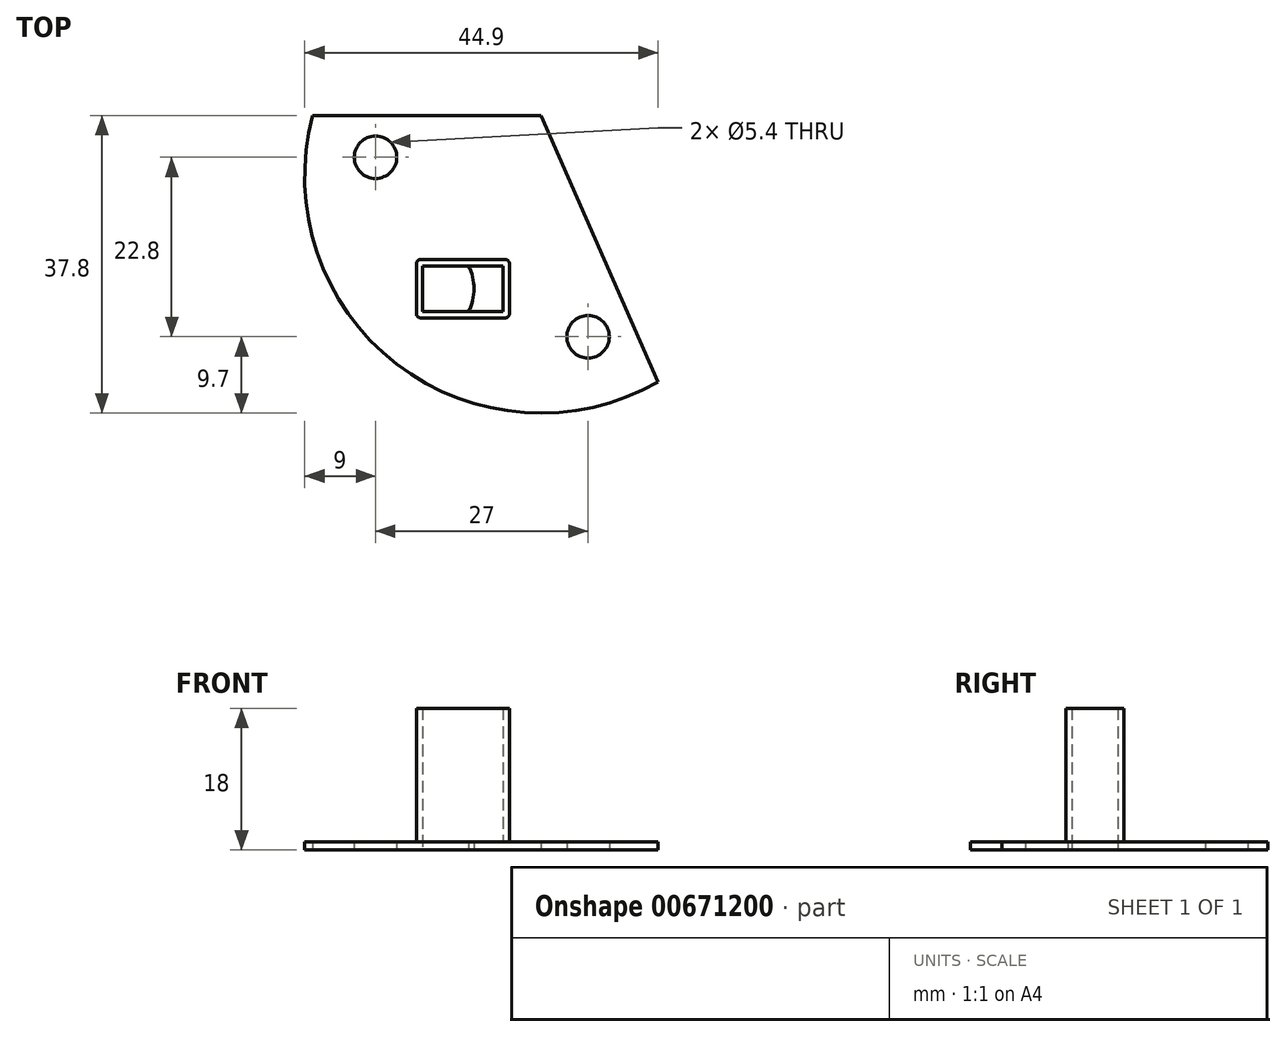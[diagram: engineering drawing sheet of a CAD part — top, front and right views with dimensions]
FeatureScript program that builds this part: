
annotation { "Feature Type Name" : "Feature", "Feature Type Description" : "" }
export const myFeature = defineFeature(function(context is Context, id is Id, definition is map)
    precondition{}
    {
        {
            var Q0;
            Q0=qCreatedBy(makeId("Top.planeOp"),FACE);
            var sketch = newSketch(context, id + "F0", { "sketchPlane" : qUnion([Q0])});
            skArc(sketch, "E0", {"start": v(-28.97, 7.8) * mm, "mid": v(-18.32, -23.75) * mm, "end": v(14.9, -26.04) * mm});
            skCircle(sketch, "E1", {"center": v(-21, 2.5) * mm, "radius": 2.7 * mm});
            skCircle(sketch, "E2", {"center": v(6, -20.3) * mm, "radius": 2.7 * mm});
            skCircle(sketch, "E3", {"center": v(-15, -14.2) * mm, "radius": 6.5 * mm});
            skLineSegment(sketch, "E4", {"start": v(-28.97, 7.8) * mm, "end": v(0, 7.8) * mm});
            skLineSegment(sketch, "E5", {"start": v(0, 7.8) * mm, "end": v(14.9, -26.04) * mm});
            skLineSegment(sketch, "E6.bottom", {"start": v(-15, -11.3) * mm, "end": v(-4.8, -11.3) * mm});
            skLineSegment(sketch, "E6.top", {"start": v(-15, -17.1) * mm, "end": v(-4.8, -17.1) * mm});
            skLineSegment(sketch, "E6.left", {"start": v(-15, -11.3) * mm, "end": v(-15, -17.1) * mm});
            skLineSegment(sketch, "E6.right", {"start": v(-4.8, -11.3) * mm, "end": v(-4.8, -17.1) * mm});
            skLineSegment(sketch, "E7.0", {"start": v(-4, -11) * mm, "end": v(-4, -17.4) * mm});
            skLineSegment(sketch, "E7.1", {"start": v(-15.3, -10.5) * mm, "end": v(-4.5, -10.5) * mm});
            skLineSegment(sketch, "E7.2", {"start": v(-15.8, -11) * mm, "end": v(-15.8, -17.4) * mm});
            skLineSegment(sketch, "E7.3", {"start": v(-15.3, -17.9) * mm, "end": v(-4.5, -17.9) * mm});
            skPoint(sketch, "E8.visualSharp", {"position": v(-15.8, -10.5) * mm});
            skArc(sketch, "E8.filletArc", {"start": v(-15.3, -10.5) * mm, "mid": v(-15.65, -10.65) * mm, "end": v(-15.8, -11) * mm});
            skPoint(sketch, "E9.visualSharp", {"position": v(-15.8, -17.9) * mm});
            skArc(sketch, "E9.filletArc", {"start": v(-15.8, -17.4) * mm, "mid": v(-15.65, -17.75) * mm, "end": v(-15.3, -17.9) * mm});
            skPoint(sketch, "E10.visualSharp", {"position": v(-4, -17.9) * mm});
            skArc(sketch, "E10.filletArc", {"start": v(-4.5, -17.9) * mm, "mid": v(-4.15, -17.75) * mm, "end": v(-4, -17.4) * mm});
            skPoint(sketch, "E11.visualSharp", {"position": v(-4, -10.5) * mm});
            skArc(sketch, "E11.filletArc", {"start": v(-4, -11) * mm, "mid": v(-4.15, -10.65) * mm, "end": v(-4.5, -10.5) * mm});
            skSolve(sketch);
        }
        {
            var Q0;
            Q0=makeQuery(id+"F0.imprint","IMPRINT",FACE,{"disambiguationData":[TD([[makeQuery(id+"F0.imprint","IMPRINT",EDGE,{"derivedFrom":sQuery(id+"F0.wireOp",EDGE,"E0")}),1.0]])]});
            var Q1;
            Q1=makeQuery(id+"F0.imprint","IMPRINT",FACE,{"disambiguationData":[TD([[makeQuery(id+"F0.imprint","IMPRINT",EDGE,{"derivedFrom":sQuery(id+"F0.wireOp",EDGE,"E7.2")}),-1.0]])]});
            var Q2;
            {var subQ0=sQuery(id+"F0.wireOp",EDGE,"E6.left");Q2=makeQuery(id+"F0.imprint","IMPRINT",FACE,{"disambiguationData":[TD([[makeQuery(id+"F0.imprint","IMPRINT",EDGE,{"derivedFrom":subQ0}),-1.0]])]});}
            var Q3;
            Q3=makeQuery(id+"F0.imprint","IMPRINT",FACE,{"disambiguationData":[TD([[makeQuery(id+"F0.imprint","IMPRINT",EDGE,{"derivedFrom":sQuery(id+"F0.wireOp",EDGE,"E7.0")}),-1.0]])]});
            var Q4;
            {var subQ0=sQuery(id+"F0.wireOp",EDGE,"E6.bottom");var subQ1=sQuery(id+"F0.wireOp",EDGE,"E3");var subQ2=makeQuery(id+"F0.imprint","INTERSECT",VERTEX,{"derivedFrom":[subQ1,subQ0]});Q4=makeQuery(id+"F0.imprint","IMPRINT",FACE,{"disambiguationData":[TD([[makeQuery(id+"F0.imprint","IMPRINT",EDGE,{"disambiguationData":[TD([[subQ2,1.0]])],"derivedFrom":subQ1}),-1.0]])]});}
            var Q5;
            {var subQ0=sQuery(id+"F0.wireOp",EDGE,"E6.right");var subQ1=sQuery(id+"F0.wireOp",EDGE,"E3");var subQ2=makeQuery(id+"F0.imprint","INTERSECT",VERTEX,{"disambiguationData":[OD(0.0)],"derivedFrom":[subQ1,subQ0]});Q5=makeQuery(id+"F0.imprint","IMPRINT",FACE,{"disambiguationData":[TD([[makeQuery(id+"F0.imprint","IMPRINT",EDGE,{"disambiguationData":[TD([[subQ2,1.0]])],"derivedFrom":subQ1}),1.0]])]});}
            var Q6;
            {var subQ0=sQuery(id+"F0.wireOp",EDGE,"E6.top");var subQ1=sQuery(id+"F0.wireOp",EDGE,"E3");var subQ2=makeQuery(id+"F0.imprint","INTERSECT",VERTEX,{"derivedFrom":[subQ1,subQ0]});Q6=makeQuery(id+"F0.imprint","IMPRINT",FACE,{"disambiguationData":[TD([[makeQuery(id+"F0.imprint","IMPRINT",EDGE,{"disambiguationData":[TD([[subQ2,-1.0]])],"derivedFrom":subQ1}),-1.0]])]});}
            extrude(context, id + "F1", {"entities" : qUnion([Q0, Q1, Q2, Q3, Q4, Q5, Q6]), "depth" : 1 * mm, "offsetDistance" : 25 * mm});
        }
        {
            var Q0;
            {var subQ0=sQuery(id+"F0.wireOp",EDGE,"E6.left");Q0=makeQuery(id+"F0.imprint","IMPRINT",FACE,{"disambiguationData":[TD([[makeQuery(id+"F0.imprint","IMPRINT",EDGE,{"derivedFrom":subQ0}),-1.0]])]});}
            var Q1;
            Q1=makeQuery(id+"F0.imprint","IMPRINT",FACE,{"disambiguationData":[TD([[makeQuery(id+"F0.imprint","IMPRINT",EDGE,{"derivedFrom":sQuery(id+"F0.wireOp",EDGE,"E7.0")}),-1.0]])]});
            var Q2;
            {var subQ0=sQuery(id+"F0.wireOp",EDGE,"E6.right");var subQ1=sQuery(id+"F0.wireOp",EDGE,"E3");var subQ2=makeQuery(id+"F0.imprint","INTERSECT",VERTEX,{"disambiguationData":[OD(0.0)],"derivedFrom":[subQ1,subQ0]});Q2=makeQuery(id+"F0.imprint","IMPRINT",FACE,{"disambiguationData":[TD([[makeQuery(id+"F0.imprint","IMPRINT",EDGE,{"disambiguationData":[TD([[subQ2,1.0]])],"derivedFrom":subQ1}),1.0]])]});}
            extrude(context, id + "F2", {"entities" : qUnion([Q0, Q1, Q2]), "operationType" : NewBodyOperationType.ADD, "depth" : 18 * mm, "offsetDistance" : 25 * mm});
        }
    });
